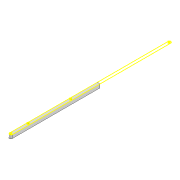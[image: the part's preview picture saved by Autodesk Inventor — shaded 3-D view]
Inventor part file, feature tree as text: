
AUTODESK INVENTOR PART (.ipt)
format: ipt  version: 2022 (Build 260153000, 153)  size: 108,032 bytes
history: native  units: mm
features: sketch x3, extrude x2, projected_geometry x1
ambient origin geometry x8: Origin, YZ Plane, XZ Plane, XY Plane, X Axis, Y Axis, Z Axis, Center Point
bodies: Solid1 (feature_tree)
feature tree (6):
  extrude  "Extrusion1"  Depth=6.0mm
  sketch  "Sketch2"  dims[d2=3.0mm d3=3.0mm]
  extrude  "Extrusion2"  Depth=3.0mm
  sketch  "Sketch1"  dims[d0=347.765mm d1=6.0mm]
  projected_geometry  "Projected Loop1"
  sketch  "Sketch3"  dims[d4=8.0mm d5=0.0mm d6=3.0mm d7=131.233mm d8=3.0mm d9=37.934mm d10=10.0mm d11=0.0mm]
